# Revit family: Track-Sliding-Krown_Lab-Oden
name_source: partatom
category: Doors
revit_build: Autodesk Revit MEP 2012 (Build: 20110916_2132(x64)
units: mm (PartAtom-declared; Revit-internal decimal feet)

## types (8) — shared parameters
Date Last Modified = 6/26/13
Description = See Part Description
Equipment Abbreviation = DR
Family Version = 1.0.0
Manufacturer = Krown Lab
Model = See Part Number
Model Disclaimer = For More Information, Contact Krown Lab
Product Documentation Link = http://www.krownlab.com
Product Page URL = http://www.krownlab.com
Provide Feedback = https://www.surveymonkey.com
Type Comments = To Modify the Panel, edit the nested Panel Family and reload into the Door
URL = http://www.krownlab.com

## per-type parameters (varying)
| type | Handle Material | Product Material | z Handle Material | z Handle Material Rail | z Track Length | z Trolley Material | z Type | z Type Material |
| Bamboo, 70" | Stainless Steel - Krown Lab - Brushed | Bamboo - Krown Lab | Stainless Steel - Krown Lab - Brushed | Bamboo - Krown Lab | 70 " | Stainless Steel - Krown Lab - Brushed | 1 | 1 |
| Bamboo, 94" | Stainless Steel - Krown Lab - Brushed | Bamboo - Krown Lab | Stainless Steel - Krown Lab - Brushed | Bamboo - Krown Lab | 94 " | Stainless Steel - Krown Lab - Brushed | 2 | 1 |
| Stainless Steel, Brushed, 94" | Stainless Steel - Krown Lab - Brushed | Stainless Steel - Krown Lab - Brushed | Stainless Steel - Krown Lab - Brushed | Stainless Steel - Krown Lab - Brushed | 94 " | Stainless Steel - Krown Lab - Brushed | 2 | 3 |
| Stainless Steel, Black, 94" | Stainless Steel - Krown Lab - Black | Stainless Steel - Krown Lab - Black | Stainless Steel - Krown Lab - Black | Stainless Steel - Krown Lab - Black | 94 " | Stainless Steel - Krown Lab - Black | 2 | 4 |
| Stainless Steel, Polished, 94" | Stainless Steel - Krown Lab - Polished | Stainless Steel - Krown Lab - Polished | Stainless Steel - Krown Lab - Polished | Stainless Steel - Krown Lab - Polished | 94 " | Stainless Steel - Krown Lab - Polished | 2 | 2 |
| Stainless Steel, Brushed, 70" | Stainless Steel - Krown Lab - Brushed | Stainless Steel - Krown Lab - Brushed | Stainless Steel - Krown Lab - Brushed | Stainless Steel - Krown Lab - Brushed | 70 " | Stainless Steel - Krown Lab - Brushed | 1 | 3 |
| Stainless Steel, Black, 70" | Stainless Steel - Krown Lab - Black | Stainless Steel - Krown Lab - Black | Stainless Steel - Krown Lab - Black | Stainless Steel - Krown Lab - Black | 70 " | Stainless Steel - Krown Lab - Black | 1 | 4 |
| Stainless Steel, Polished, 70" | Stainless Steel - Krown Lab - Polished | Stainless Steel - Krown Lab - Polished | Stainless Steel - Krown Lab - Polished | Stainless Steel - Krown Lab - Polished | 70 " | Stainless Steel - Krown Lab - Polished | 1 | 2 |

## geometry (parser evidence)
native form markers: Blend x11, Sweep x8
no freeform markers — native parametric forms only
